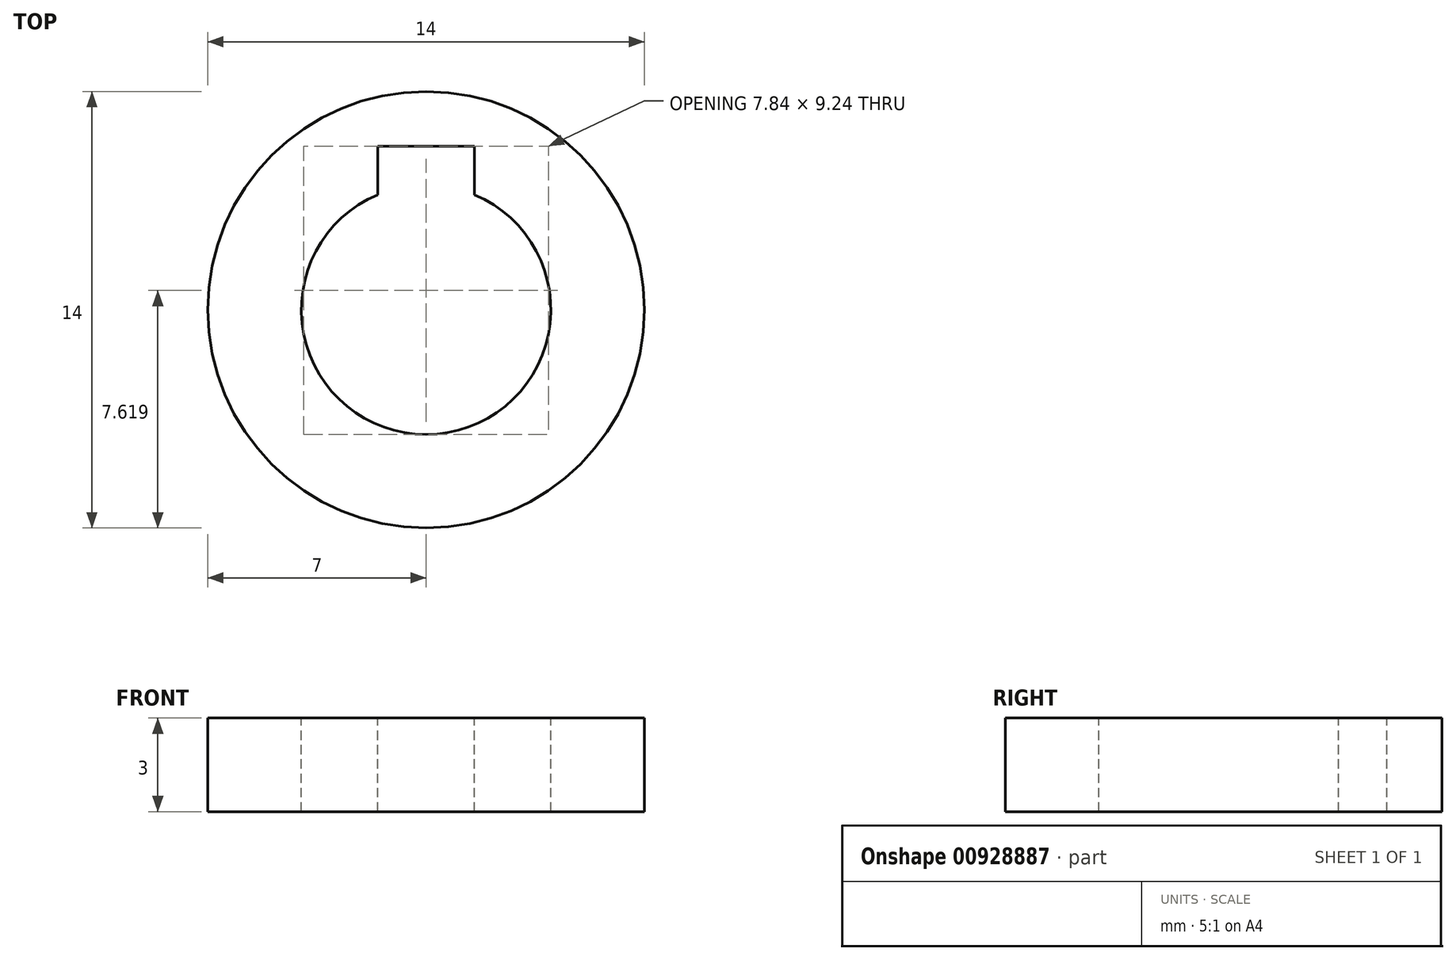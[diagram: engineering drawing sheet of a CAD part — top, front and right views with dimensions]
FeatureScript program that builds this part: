
annotation { "Feature Type Name" : "Feature", "Feature Type Description" : "" }
export const myFeature = defineFeature(function(context is Context, id is Id, definition is map)
    precondition{}
    {
        {
            var Q0;
            Q0=qCreatedBy(makeId("Top.planeOp"),FACE);
            var sketch = newSketch(context, id + "F0", { "sketchPlane" : qUnion([Q0])});
            skCircle(sketch, "E0", {"center": v(0, 0) * mm, "radius": 7 * mm});
            skSolve(sketch);
        }
        {
            var Q0;
            Q0=qSketchRegion(id+"F0",true);
            extrude(context, id + "F1", {"entities" : qUnion([Q0]), "depth" : 3 * mm, "offsetDistance" : 25 * mm});
        }
        {
            var Q0;
            Q0=makeQuery(id+"F1.opExtrude","CAP_FACE",FACE,{"disambiguationData":[OSD([sQuery(id+"F0.wireOp",EDGE,"E0")])],"isStart":false});
            var sketch = newSketch(context, id + "F2", { "sketchPlane" : qUnion([Q0])});
            skCircle(sketch, "E1", {"center": v(0, 0) * mm, "radius": 4 * mm});
            skLineSegment(sketch, "E2", {"start": v(0, 4) * mm, "end": v(0, 5.24) * mm, "construction": true});
            skLineSegment(sketch, "E3", {"start": v(0, 5.24) * mm, "end": v(1.55, 5.24) * mm});
            skLineSegment(sketch, "E4", {"start": v(1.55, 5.24) * mm, "end": v(1.55, 3.69) * mm});
            skLineSegment(sketch, "E5.MirrorCS", {"start": v(0, 5.24) * mm, "end": v(-1.55, 5.24) * mm});
            skLineSegment(sketch, "E6.MirrorCS", {"start": v(-1.55, 5.24) * mm, "end": v(-1.55, 3.69) * mm});
            skSolve(sketch);
        }
        {
            var Q0;
            Q0=qSketchRegion(id+"F2",true);
            var Q1;
            Q1=makeQuery(id+"F1.opExtrude","CAP_FACE",FACE,{"disambiguationData":[OSD([sQuery(id+"F0.wireOp",EDGE,"E0")])],"isStart":true});
            extrude(context, id + "F3", {"entities" : qUnion([Q0]), "operationType" : NewBodyOperationType.REMOVE, "endBound" : BoundingType.UP_TO_SURFACE, "oppositeDirection" : true, "depth" : 25 * mm, "endBoundEntityFace" : qUnion([Q1]), "offsetDistance" : 25 * mm});
        }
    });
